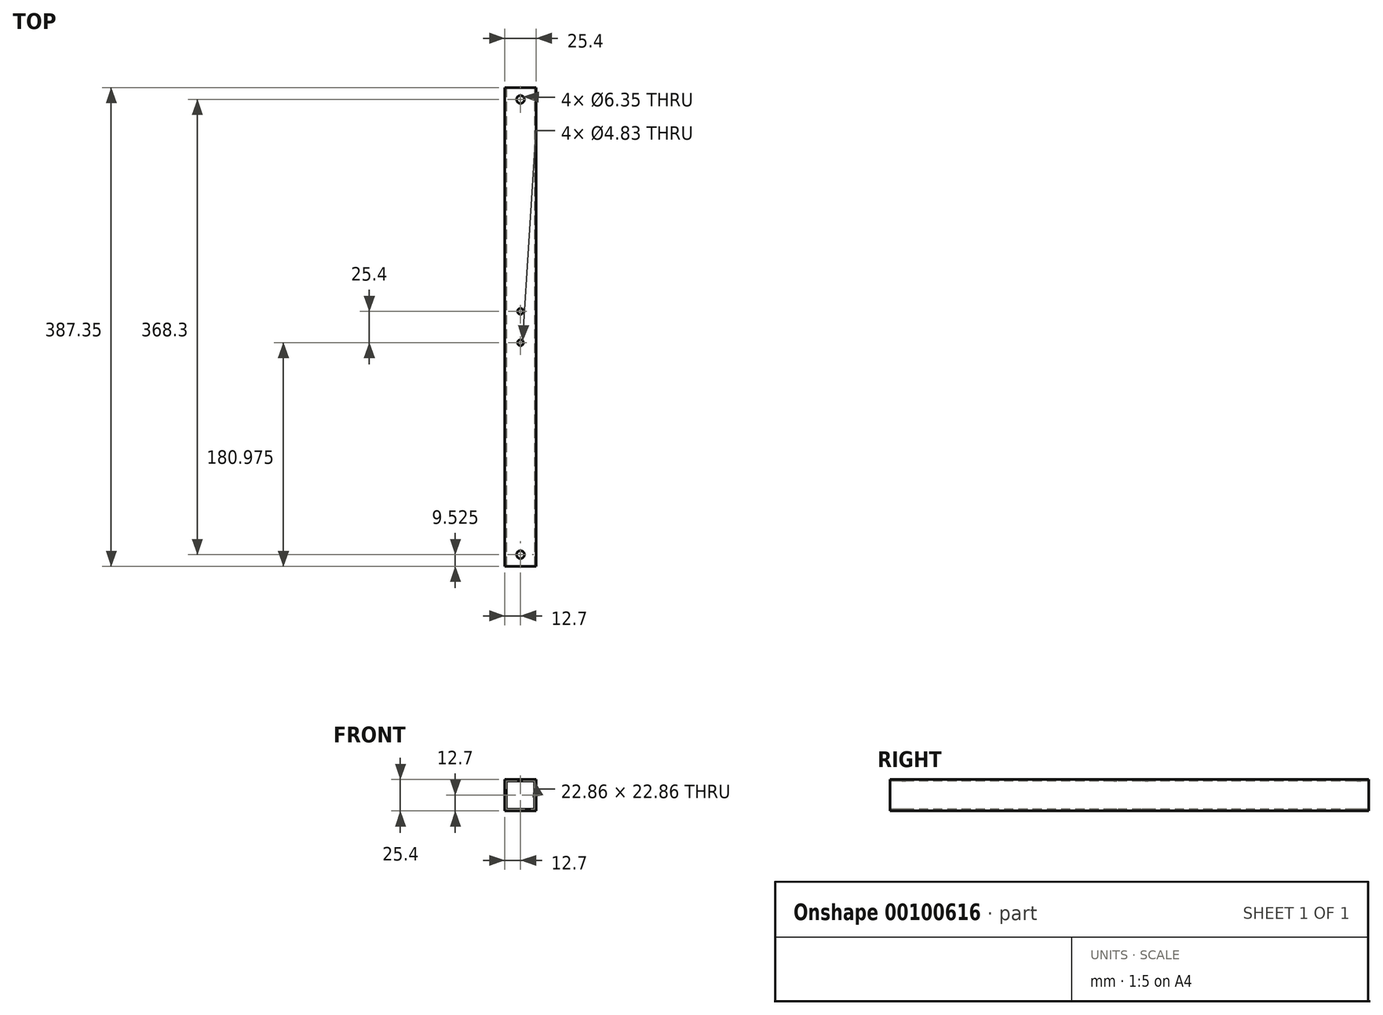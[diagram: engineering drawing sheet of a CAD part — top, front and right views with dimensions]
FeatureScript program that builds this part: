
annotation { "Feature Type Name" : "Feature", "Feature Type Description" : "" }
export const myFeature = defineFeature(function(context is Context, id is Id, definition is map)
    precondition{}
    {
        {
            var Q0;
            Q0=qCreatedBy(makeId("Front.planeOp"),FACE);
            var sketch = newSketch(context, id + "F0", { "sketchPlane" : qUnion([Q0])});
            skLineSegment(sketch, "E0.bottom", {"start": v(-12.7, 12.7) * mm, "end": v(12.7, 12.7) * mm});
            skLineSegment(sketch, "E0.top", {"start": v(-12.7, -12.7) * mm, "end": v(12.7, -12.7) * mm});
            skLineSegment(sketch, "E0.left", {"start": v(-12.7, 12.7) * mm, "end": v(-12.7, -12.7) * mm});
            skLineSegment(sketch, "E0.right", {"start": v(12.7, 12.7) * mm, "end": v(12.7, -12.7) * mm});
            skPoint(sketch, "E1", {"position": v(0, 12.7) * mm});
            skPoint(sketch, "E2", {"position": v(12.7, 0) * mm});
            skLineSegment(sketch, "E3.0", {"start": v(-11.43, 11.43) * mm, "end": v(11.43, 11.43) * mm});
            skLineSegment(sketch, "E3.1", {"start": v(-11.43, 11.43) * mm, "end": v(-11.43, -11.43) * mm});
            skLineSegment(sketch, "E3.2", {"start": v(-11.43, -11.43) * mm, "end": v(11.43, -11.43) * mm});
            skLineSegment(sketch, "E3.3", {"start": v(11.43, 11.43) * mm, "end": v(11.43, -11.43) * mm});
            skSolve(sketch);
        }
        {
            var Q0;
            Q0=makeQuery(id+"F0.imprint","IMPRINT",FACE,{"disambiguationData":[TD([[makeQuery(id+"F0.imprint","IMPRINT",EDGE,{"derivedFrom":sQuery(id+"F0.wireOp",EDGE,"E0.bottom")}),-1.0]])]});
            extrude(context, id + "F1", {"entities" : qUnion([Q0]), "oppositeDirection" : true, "depth" : 387.35 * mm});
        }
        {
            var Q0;
            Q0=makeQuery(id+"F1.opExtrude","SWEPT_FACE",FACE,{"disambiguationData":[OSD([sQuery(id+"F0.wireOp",EDGE,"E0.bottom")])]});
            var sketch = newSketch(context, id + "F2", { "sketchPlane" : qUnion([Q0])});
            skPoint(sketch, "E4.center.orphan", {"position": v(0, 9.53) * mm});
            skLineSegment(sketch, "E5", {"start": v(-12.7, 193.68) * mm, "end": v(12.7, 193.68) * mm, "construction": true});
            skPoint(sketch, "E6.MirrorP", {"position": v(0, 377.83) * mm});
            skCircle(sketch, "E7", {"center": v(0, 9.53) * mm, "radius": 3.18 * mm});
            skCircle(sketch, "E8.MirrorC", {"center": v(0, 377.83) * mm, "radius": 3.18 * mm});
            skCircle(sketch, "E9", {"center": v(0, 180.98) * mm, "radius": 2.41 * mm});
            skPoint(sketch, "E9.centerSnap0", {"position": v(0, 193.68) * mm});
            skCircle(sketch, "E10.MirrorC", {"center": v(0, 206.38) * mm, "radius": 2.41 * mm});
            skSolve(sketch);
        }
        {
            var Q0;
            Q0 = qSketchRegion(id + "F2", true);
            extrude(context, id + "F3", {"entities" : qUnion([Q0]), "operationType" : NewBodyOperationType.REMOVE, "endBound" : BoundingType.THROUGH_ALL, "oppositeDirection" : true, "depth" : 25.4 * mm});
        }
    });
